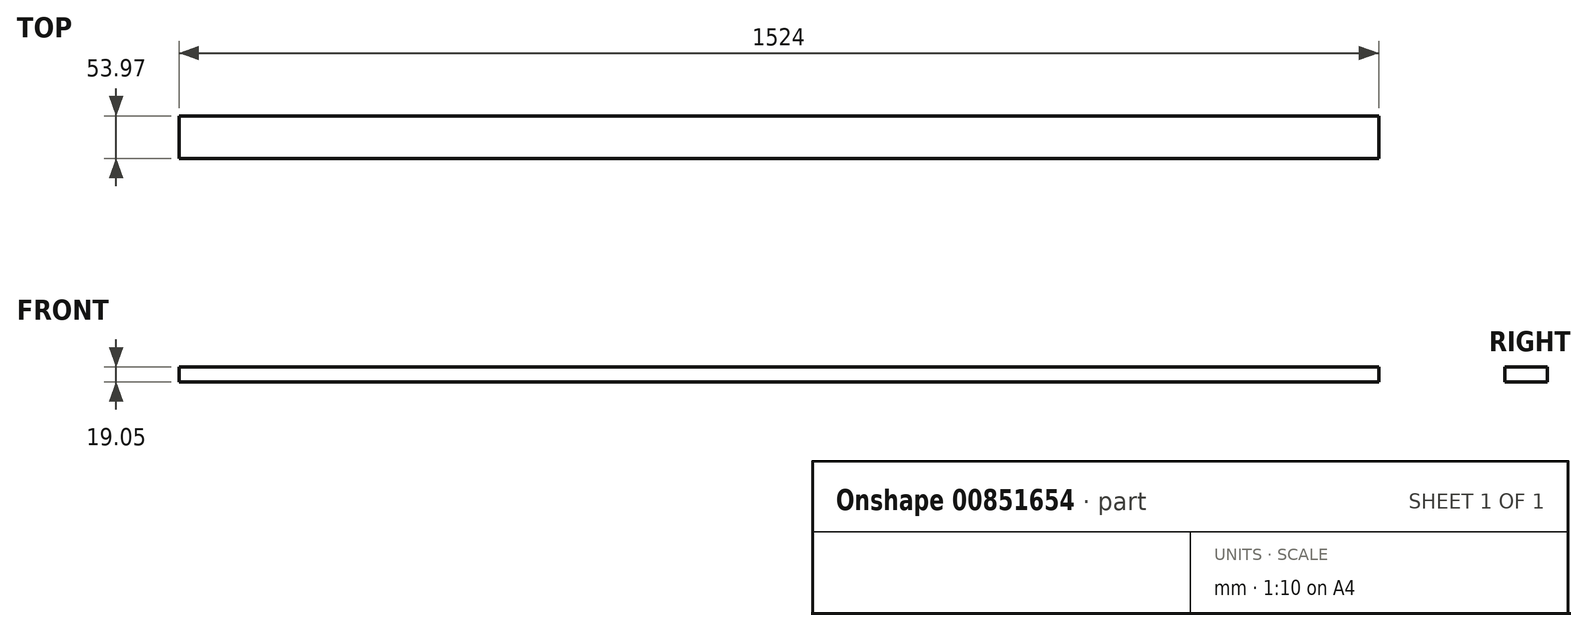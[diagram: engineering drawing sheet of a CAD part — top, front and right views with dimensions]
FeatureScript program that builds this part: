
annotation { "Feature Type Name" : "Feature", "Feature Type Description" : "" }
export const myFeature = defineFeature(function(context is Context, id is Id, definition is map)
    precondition{}
    {
        {
            var Q0;
            Q0=qCreatedBy(makeId("Top.planeOp"),FACE);
            var sketch = newSketch(context, id + "F0", { "sketchPlane" : qUnion([Q0])});
            skLineSegment(sketch, "E0", {"start": v(-365.3, 35.23) * mm, "end": v(1158.7, 35.23) * mm});
            skLineSegment(sketch, "E1", {"start": v(1158.7, 35.23) * mm, "end": v(1158.7, -18.74) * mm});
            skLineSegment(sketch, "E2", {"start": v(1158.7, -18.74) * mm, "end": v(-365.3, -18.74) * mm});
            skLineSegment(sketch, "E3", {"start": v(-365.3, -18.74) * mm, "end": v(-365.3, 35.23) * mm});
            skSolve(sketch);
        }
        {
            var Q0;
            Q0 = qSketchRegion(id + "F0", true);
            extrude(context, id + "F1", {"entities" : qUnion([Q0]), "depth" : 19.05 * mm, "offsetDistance" : 25.4 * mm});
        }
    });
